# Revit family: S-797
name_source: partatom
category: Aparatos sanitarios
revit_build: Autodesk Revit 2015 (Build: 20140606_1530(x64)
units: mm (PartAtom-declared; Revit-internal decimal feet)

## types (2) — shared parameters
Altura total mínima = 115-125mm
Caudal = 0.8 L/s
Comentarios de tipo = CON FIJACION A PARED, CON PRENSATELAS PARA LÁMINAS IMPERMEABILIZANTES GEOTEXTILES O DE PVC. CON PROTECCION DE OBRA.  CON REJILLA REGULABLE EN ALTURA.
Descripción = SUMIDERO TRIANGULAR PARA PLATOS DE DUCHA DE OBRA EN ESQUINA, SIFON ORIENTABLE, SALIDA HORIZONTAL, CON REJILLA DROPS, REGULACION DE ALTURA
Dmax = 26 mm
Dmin = 10 mm  [stored 0.0328084 ft]
E = 40 mm  [stored 0.131234 ft]
F = 50 mm  [stored 0.164042 ft]
Fabricante = Jimten
Hmax = 16 mm  [stored 0.0524934 ft]
Hmin = 6 mm  [stored 0.019685 ft]
Material = ABS
Medida = 236mm x 331mm x 236 mm
Modelo = S-797
Rejilla = INOX AISI304
Sello hidráulico = 50 mm
URL = http://www.jimten.com
WFU = 1

## per-type parameters (varying)
| type | Referencia | Salida |
| S-797_40_DROPS | 13374 | 40H |
| S-797_40-50_DROPS | 13375 | 40M/50M |

note: [stored X ft] marks values corroborated as IEEE doubles in the binary element streams (Revit-internal decimal feet)

## geometry (parser evidence)
native form markers: Blend x3, Sweep x14
no freeform markers — native parametric forms only
